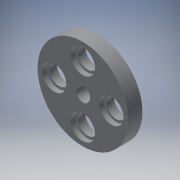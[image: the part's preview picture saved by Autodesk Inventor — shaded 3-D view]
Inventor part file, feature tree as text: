
AUTODESK INVENTOR PART (.ipt)
format: ipt  version: 2017 (Build 210142000, 142)  size: 171,520 bytes
history: native  units: mm
features: extrude x4, sketch x4
ambient origin geometry x8: Origin, YZ Plane, XZ Plane, XY Plane, X Axis, Y Axis, Z Axis, Center Point
bodies: Solide1 (feature_tree)
feature tree (8):
  extrude  "Extrusion1"  Depth=4.1mm
  extrude  "Extrusion2"  Depth=6.0mm
  extrude  "Extrusion3"  Depth=3.0mm TaperAngle=0.0deg
  extrude  "Extrusion4"  Depth=3.0mm
  sketch  "Esquisse1"
  sketch  "Esquisse2"
  sketch  "Sketch3"  dims[d0=19.0mm d1=4.1mm]
  sketch  "Sketch4"  dims[d2=20.0mm d4=6.0mm d5=20.0mm d7=6.0mm d10=20.0mm d12=6.0mm d13=20.0mm d15=6.0mm d18=3.0mm d19=0.0mm d20=3.0mm d21=10.0mm d22=0.0mm d23=5.1mm d24=5.1mm d25=5.1mm d26=5.1mm d27=1.0mm d28=0.0mm d29=1.0mm d30=0.0mm]
